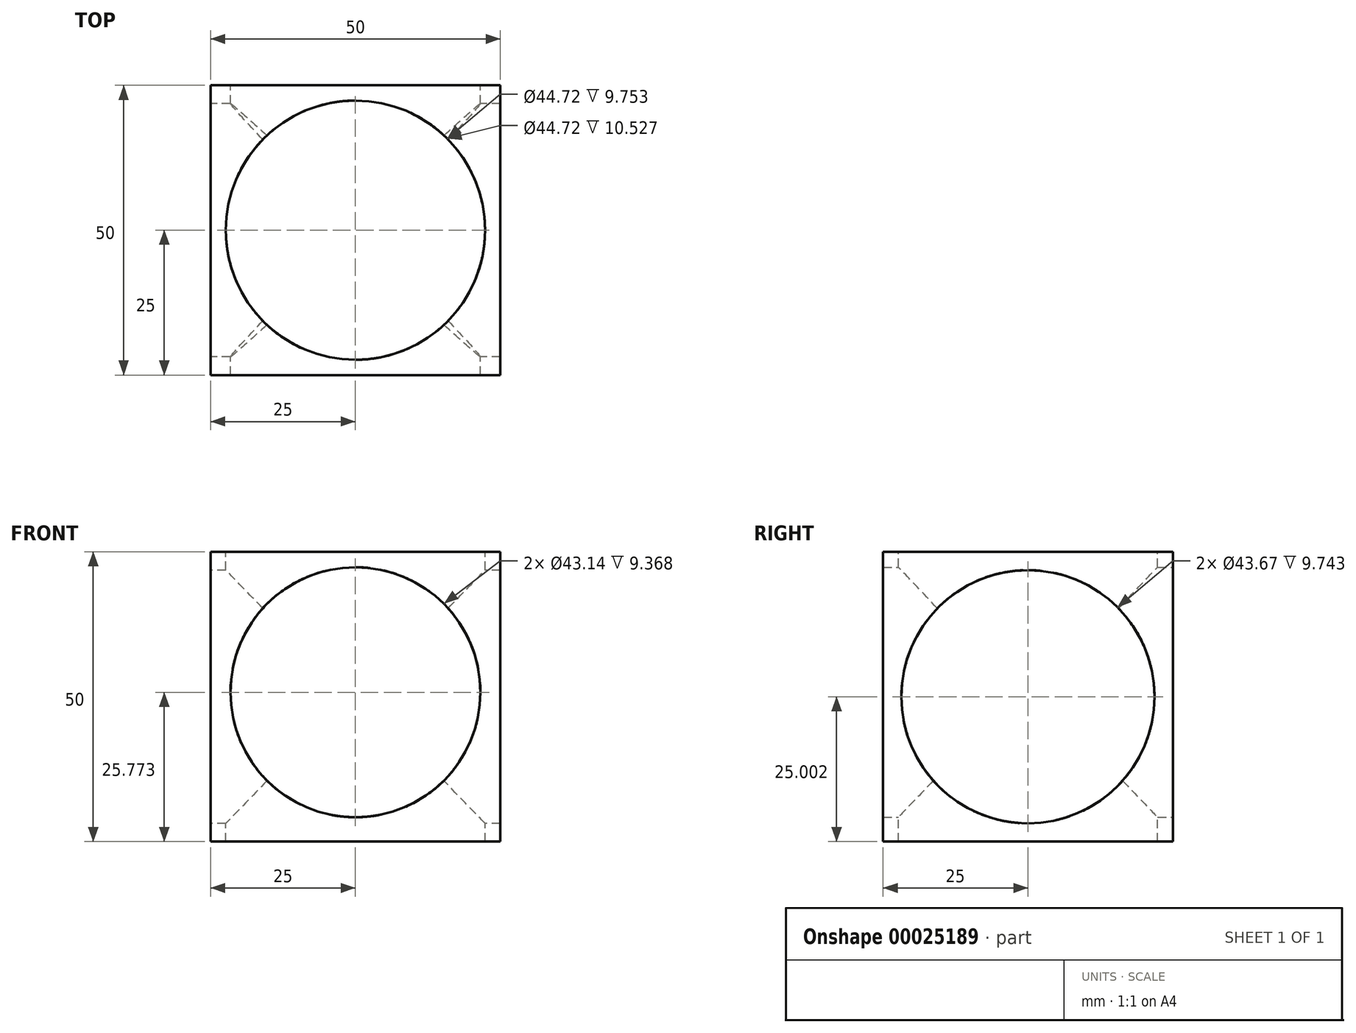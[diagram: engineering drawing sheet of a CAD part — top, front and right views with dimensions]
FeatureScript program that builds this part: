
annotation { "Feature Type Name" : "Feature", "Feature Type Description" : "" }
export const myFeature = defineFeature(function(context is Context, id is Id, definition is map)
    precondition{}
    {
        {
            var Q0;
            Q0=qCreatedBy(makeId("Top.planeOp"),FACE);
            var sketch = newSketch(context, id + "F0", { "sketchPlane" : qUnion([Q0])});
            skLineSegment(sketch, "E0.rect.bottom", {"start": v(-25, 25) * mm, "end": v(25, 25) * mm});
            skLineSegment(sketch, "E0.rect.top", {"start": v(-25, -25) * mm, "end": v(25, -25) * mm});
            skLineSegment(sketch, "E0.rect.left", {"start": v(-25, 25) * mm, "end": v(-25, -25) * mm});
            skLineSegment(sketch, "E0.rect.right", {"start": v(25, 25) * mm, "end": v(25, -25) * mm});
            skPoint(sketch, "E0.rect.middle", {"position": v(0, 0) * mm});
            skSolve(sketch);
        }
        {
            var Q0;
            Q0=makeQuery(id+"F0.imprint","IMPRINT",FACE,{"disambiguationData":[TD([[makeQuery(id+"F0.imprint","IMPRINT",EDGE,{"derivedFrom":sQuery(id+"F0.wireOp",EDGE,"E0.rect.bottom")}),-1.0]])]});
            extrude(context, id + "F1", {"entities" : qUnion([Q0]), "depth" : 50 * mm});
        }
        {
            var Q0;
            Q0=makeQuery(id+"F1.opExtrude","CAP_FACE",FACE,{"disambiguationData":[OSD([sQuery(id+"F0.wireOp",EDGE,"E0.rect.bottom"),sQuery(id+"F0.wireOp",EDGE,"E0.rect.top"),sQuery(id+"F0.wireOp",EDGE,"E0.rect.left"),sQuery(id+"F0.wireOp",EDGE,"E0.rect.right")])],"isStart":false});
            var sketch = newSketch(context, id + "F2", { "sketchPlane" : qUnion([Q0])});
            skCircle(sketch, "E1", {"center": v(0, 0) * mm, "radius": 22.36 * mm});
            skSolve(sketch);
        }
        {
            var Q0;
            Q0=makeQuery(id+"F2.imprint","IMPRINT",FACE,{"disambiguationData":[TD([[makeQuery(id+"F2.imprint","IMPRINT",EDGE,{"derivedFrom":sQuery(id+"F2.wireOp",EDGE,"E1")}),1.0]])]});
            extrude(context, id + "F3", {"entities" : qUnion([Q0]), "operationType" : NewBodyOperationType.REMOVE, "oppositeDirection" : true, "depth" : 50 * mm});
        }
        {
            var Q0;
            Q0=makeQuery(id+"F1.opExtrude","SWEPT_FACE",FACE,{"disambiguationData":[OSD([sQuery(id+"F0.wireOp",EDGE,"E0.rect.bottom")])]});
            var sketch = newSketch(context, id + "F4", { "sketchPlane" : qUnion([Q0])});
            skCircle(sketch, "E2", {"center": v(0, 25.77) * mm, "radius": 21.57 * mm});
            skSolve(sketch);
        }
        {
            var Q0;
            Q0=makeQuery(id+"F4.imprint","IMPRINT",FACE,{"disambiguationData":[TD([[makeQuery(id+"F4.imprint","IMPRINT",EDGE,{"derivedFrom":sQuery(id+"F4.wireOp",EDGE,"E2")}),1.0]])]});
            extrude(context, id + "F5", {"entities" : qUnion([Q0]), "operationType" : NewBodyOperationType.REMOVE, "oppositeDirection" : true, "depth" : 50 * mm});
        }
        {
            var Q0;
            Q0=makeQuery(id+"F1.opExtrude","SWEPT_FACE",FACE,{"disambiguationData":[OSD([sQuery(id+"F0.wireOp",EDGE,"E0.rect.left")])]});
            var sketch = newSketch(context, id + "F6", { "sketchPlane" : qUnion([Q0])});
            skCircle(sketch, "E3", {"center": v(0, 25) * mm, "radius": 21.84 * mm});
            skSolve(sketch);
        }
        {
            var Q0;
            Q0=makeQuery(id+"F6.imprint","IMPRINT",FACE,{"disambiguationData":[TD([[makeQuery(id+"F6.imprint","IMPRINT",EDGE,{"derivedFrom":sQuery(id+"F6.wireOp",EDGE,"E3")}),1.0]])]});
            extrude(context, id + "F7", {"entities" : qUnion([Q0]), "operationType" : NewBodyOperationType.REMOVE, "oppositeDirection" : true, "depth" : 50 * mm});
        }
    });
